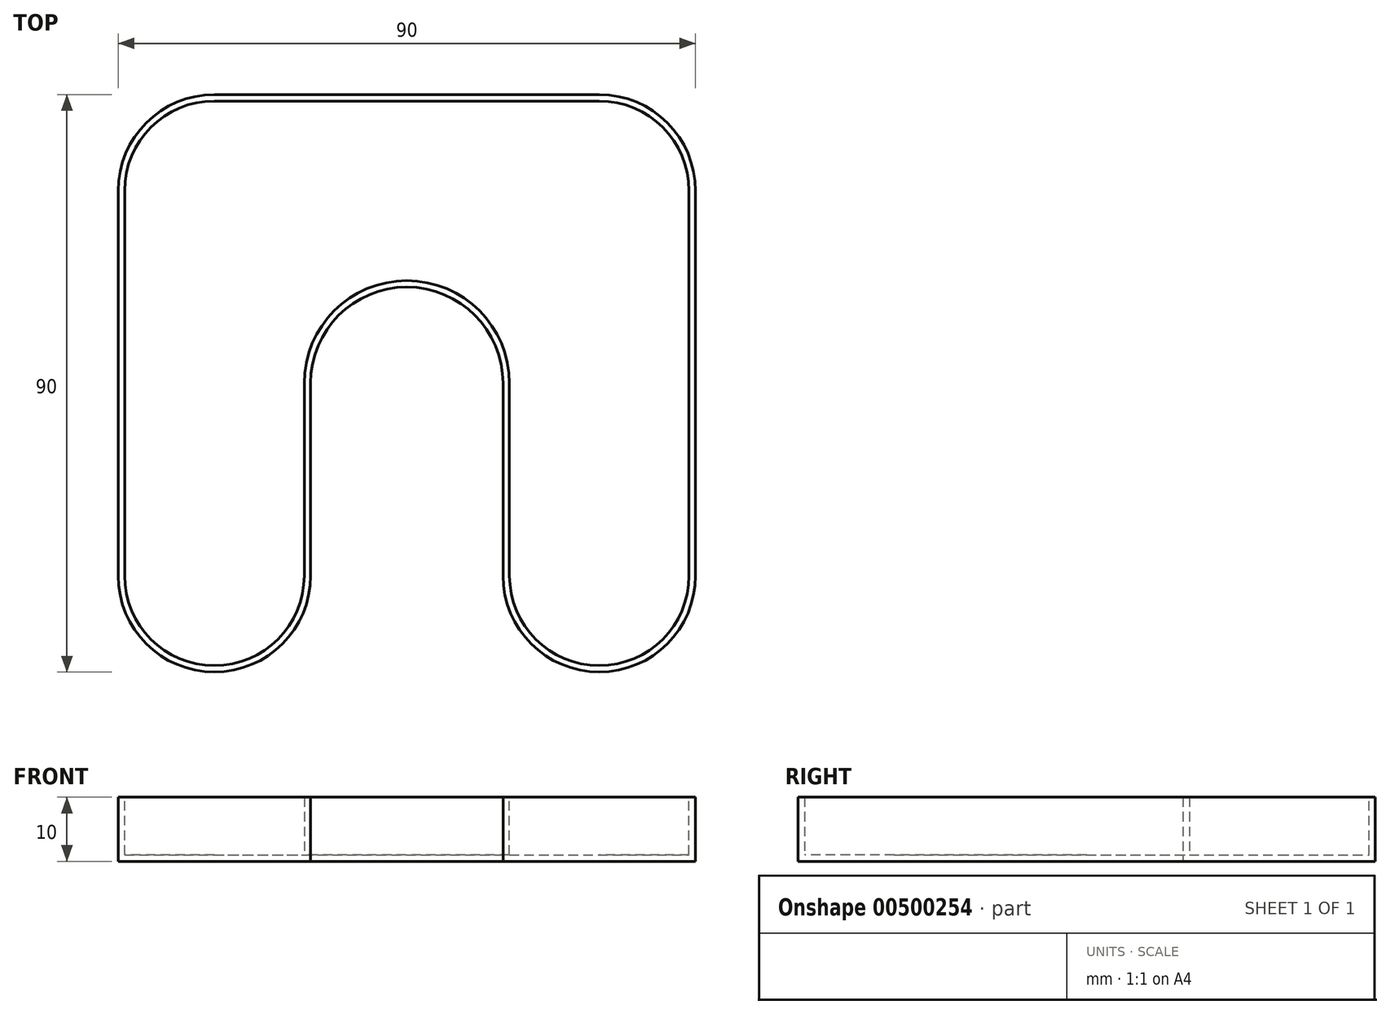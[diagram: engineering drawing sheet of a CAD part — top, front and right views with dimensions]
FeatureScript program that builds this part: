
annotation { "Feature Type Name" : "Feature", "Feature Type Description" : "" }
export const myFeature = defineFeature(function(context is Context, id is Id, definition is map)
    precondition{}
    {
        {
            var Q0;
            Q0=qCreatedBy(makeId("Top.planeOp"),FACE);
            var sketch = newSketch(context, id + "F0", { "sketchPlane" : qUnion([Q0])});
            skLineSegment(sketch, "E0", {"start": v(-51.21, -28.28) * mm, "end": v(-51.21, 31.72) * mm});
            skLineSegment(sketch, "E1", {"start": v(-36.21, 46.72) * mm, "end": v(23.79, 46.72) * mm});
            skLineSegment(sketch, "E2", {"start": v(38.79, 31.72) * mm, "end": v(38.79, -28.28) * mm});
            skLineSegment(sketch, "E3", {"start": v(23.79, -43.28) * mm, "end": v(23.79, -43.28) * mm});
            skLineSegment(sketch, "E4", {"start": v(8.79, -28.28) * mm, "end": v(8.79, 1.72) * mm});
            skLineSegment(sketch, "E5", {"start": v(-6.21, 16.72) * mm, "end": v(-6.21, 16.72) * mm});
            skLineSegment(sketch, "E6", {"start": v(-21.21, 1.72) * mm, "end": v(-21.21, -28.28) * mm});
            skLineSegment(sketch, "E7", {"start": v(-36.21, -43.28) * mm, "end": v(-36.21, -43.28) * mm});
            skPoint(sketch, "E8.visualSharp", {"position": v(-51.21, 46.72) * mm});
            skArc(sketch, "E8.filletArc", {"start": v(-36.21, 46.72) * mm, "mid": v(-46.82, 42.32) * mm, "end": v(-51.21, 31.72) * mm});
            skPoint(sketch, "E9.visualSharp", {"position": v(38.79, 46.72) * mm});
            skArc(sketch, "E9.filletArc", {"start": v(38.79, 31.72) * mm, "mid": v(34.4, 42.32) * mm, "end": v(23.79, 46.72) * mm});
            skPoint(sketch, "E10.visualSharp", {"position": v(8.79, 16.72) * mm});
            skArc(sketch, "E10.filletArc", {"start": v(8.79, 1.72) * mm, "mid": v(4.4, 12.32) * mm, "end": v(-6.21, 16.72) * mm});
            skPoint(sketch, "E11.visualSharp", {"position": v(-21.21, 16.72) * mm});
            skArc(sketch, "E11.filletArc", {"start": v(-6.21, 16.72) * mm, "mid": v(-16.82, 12.32) * mm, "end": v(-21.21, 1.72) * mm});
            skPoint(sketch, "E12.visualSharp", {"position": v(-51.21, -43.28) * mm});
            skArc(sketch, "E12.filletArc", {"start": v(-51.21, -28.28) * mm, "mid": v(-46.82, -38.89) * mm, "end": v(-36.21, -43.28) * mm});
            skPoint(sketch, "E13.visualSharp", {"position": v(-21.21, -43.28) * mm});
            skArc(sketch, "E13.filletArc", {"start": v(-36.21, -43.28) * mm, "mid": v(-25.6, -38.89) * mm, "end": v(-21.21, -28.28) * mm});
            skPoint(sketch, "E14.visualSharp", {"position": v(8.79, -43.28) * mm});
            skArc(sketch, "E14.filletArc", {"start": v(8.79, -28.28) * mm, "mid": v(13.18, -38.89) * mm, "end": v(23.79, -43.28) * mm});
            skPoint(sketch, "E15.visualSharp", {"position": v(38.79, -43.28) * mm});
            skArc(sketch, "E15.filletArc", {"start": v(23.79, -43.28) * mm, "mid": v(34.4, -38.89) * mm, "end": v(38.79, -28.28) * mm});
            skSolve(sketch);
        }
        {
            var Q0;
            Q0=qSketchRegion(id+"F0",true);
            extrude(context, id + "F1", {"entities" : qUnion([Q0]), "depth" : 10 * mm});
        }
        {
            var Q0;
            Q0=makeQuery(id+"F1.opExtrude","CAP_FACE",FACE,{"disambiguationData":[OSD([sQuery(id+"F0.wireOp",EDGE,"E0"),sQuery(id+"F0.wireOp",EDGE,"E1"),sQuery(id+"F0.wireOp",EDGE,"E2"),sQuery(id+"F0.wireOp",EDGE,"E4"),sQuery(id+"F0.wireOp",EDGE,"E6"),sQuery(id+"F0.wireOp",EDGE,"E8.filletArc"),sQuery(id+"F0.wireOp",EDGE,"E9.filletArc"),sQuery(id+"F0.wireOp",EDGE,"E10.filletArc"),sQuery(id+"F0.wireOp",EDGE,"E11.filletArc"),sQuery(id+"F0.wireOp",EDGE,"E12.filletArc"),sQuery(id+"F0.wireOp",EDGE,"E13.filletArc"),sQuery(id+"F0.wireOp",EDGE,"E14.filletArc"),sQuery(id+"F0.wireOp",EDGE,"E15.filletArc")])],"isStart":false});
            shell(context, id + "F2", {"entities" : qUnion([Q0]), "thickness" : 1 * mm});
        }
    });
